# Revit family: PV_Compact_PN25_DN080_(20-100kPa)_RFA_2018
name_source: partatom
category: Pipe Accessories
revit_build: Autodesk Revit LT 2018 (Build: 20180329_1100(x64)
units: mm (PartAtom-declared; Revit-internal decimal feet)

## family parameters
Always vertical = Yes
Cut with Voids When Loaded = No
Part Type = Valve - Breaks Into
Round Connector Dimension = Use Diameter
Shared = No
Work Plane-Based = No

## types (7) — shared parameters
CAT0 = Yes
Description = Nastavitelný regulátor tlakové diference
L2D = 230 mm
L2D_Min = 30 mm  [stored 0.0984252 ft]
MC Pressure Drop Maximum Value = 0.0 Pa
MC Pressure Drop Minimum Value = 0.0 Pa
MC Use Limits From Balancing Method = No
Manufacturer = Hydronic Systems Prague s.r.o.
QmdConnectorList = 301;D;302;D
URL = www.hydronic.cz
W2D = 50 mm  [stored 0.164042 ft]
magiPartTypeId = 304
magiProductFamilyId = 7c5767a2a396495b8f1e69654734b4
zero-valued in all types: MC Throttling Maximum Value, MC Throttling Minimum Value

## per-type parameters (varying)
| type | D | DF2 | H1 | H2 | H3 | H4 | H6 | L2 | L3 | L4 | LF | LF2 | LF__ve | MC Product Code | R1 | R3 | R4 | Type Comments | magiProductId |
| PV Compact PN25 DN050 (20-100kPa) | 50 mm | 83 mm | 124 mm | 62 mm | 21 mm | 25 mm  [stored 0.082021 ft] | 82 mm | 115 mm | 193 mm | 108 mm | 18 mm | 9 mm  [stored 0.0295276 ft] | -18 mm | 53-3320 DN050 PN25; nastavitelný rozsah dp=20~100kPa; Q=3,2~13,0 m3/h;  kvs=29 | 58 mm | 43 mm | 40 mm | PŘÍRUBOVÝ; PN25; dpmax=1000kPa; -10~+120°C | c83fbc6219d94d148ccf13b963e54b |
| PV Compact PN25 DN065 (20-100kPa) | 65 mm | 93 mm | 139 mm | 69 mm | 23 mm | 28 mm  [stored 0.0918635 ft] | 105 mm | 145 mm | 244 mm | 136 mm | 23 mm | 12 mm  [stored 0.0393701 ft] | -23 mm | 53-3323 DN065 PN25; nastavitelný rozsah dp=20~100kPa; Q=4,7~18,8 m3/h;  kvs=42 | 73 mm | 48 mm  [stored 0.15748 ft] | 51 mm | PŘÍRUBOVÝ; PN25; dpmax=1000kPa; -10~+120°C | 130d70b5f9404660882d0b277b908a |
| PV Compact PN25 DN080 (20-100kPa) | 80 mm | 100 mm | 150 mm | 75 mm | 25 mm  [stored 0.082021 ft] | 30 mm  [stored 0.0984252 ft] | 141 mm | 155 mm | 260 mm | 146 mm | 25 mm  [stored 0.082021 ft] | 12 mm  [stored 0.0393701 ft] | -25 mm | 53-3326 DN080 PN25; nastavitelný rozsah dp=20~100kPa; Q=7,5~30,0 m3/h;  kvs=67 | 78 mm | 52 mm  [stored 0.170604 ft] | 54 mm | PŘÍRUBOVÝ; PN25; dpmax=1000kPa; -10~+120°C | a1826ed98cb744f2bf0249353d27a7 |
| PV Compact PN25 DN100 (20-100kPa) | 100 mm | 118 mm | 176 mm | 88 mm | 29 mm | 35 mm | 235 mm | 175 mm | 294 mm | 165 mm | 28 mm  [stored 0.0918635 ft] | 14 mm  [stored 0.0459318 ft] | -28 mm  [stored -0.0918635 ft] | 53-3329 DN100 PN25; nastavitelný rozsah dp=20~100kPa; Q=12,9~51,4 m3/h;  kvs=115 | 88 mm | 61 mm | 61 mm | PŘÍRUBOVÝ; PN25; dpmax=1000kPa; -10~+120°C | 7cf36ffc9d0642d6874cd3d421d477 |
| PV Compact PN25 DN125 (20-100kPa) | 125 mm | 135 mm | 203 mm | 101 mm | 34 mm | 41 mm | 226 mm | 200 mm | 336 mm | 188 mm | 32 mm  [stored 0.104987 ft] | 16 mm  [stored 0.0524934 ft] | -32 mm  [stored -0.104987 ft] | 53-3332 DN125 PN25; nastavitelný rozsah dp=20~100kPa; Q=19,0~76,0 m3/h;  kvs=170 | 100 mm | 70 mm  [stored 0.229659 ft] | 70 mm  [stored 0.229659 ft] | PŘÍRUBOVÝ; PN25; dpmax=1000kPa; -10~+120°C | 79fb1938054147a099bb761cc75d0a |
| PV Compact PN25 DN150 (20-100kPa) | 150 mm | 143 mm | 214 mm | 107 mm | 36 mm | 43 mm | 256 mm | 240 mm | 403 mm | 226 mm | 38 mm | 19 mm | -38 mm | 53-3335 DN150 PN25; nastavitelný rozsah dp=20~100kPa; Q=28,0~112 m3/h;  kvs=250 | 120 mm | 74 mm | 84 mm | PŘÍRUBOVÝ; PN25; dpmax=1000kPa; -10~+110°C | 9089b5560db447c5b770287446c8b2 |
| PV Compact PN25 DN200 (20-100kPa) | 200 mm | 190 mm | 285 mm | 143 mm | 48 mm  [stored 0.15748 ft] | 57 mm | 150 mm | 300 mm | 504 mm | 282 mm | 48 mm  [stored 0.15748 ft] | 24 mm  [stored 0.0787402 ft] | -48 mm  [stored -0.15748 ft] | 53-3338 DN200 PN25; nastavitelný rozsah dp=20~100kPa; Q=30,7~123 m3/h;  kvs=275 | 150 mm | 99 mm | 105 mm | PŘÍRUBOVÝ; PN25; dpmax=1000kPa; -10~+110°C | 21d4a96559b243fabb2a9fe74f4fa1 |

note: [stored X ft] marks values corroborated as IEEE doubles in the binary element streams (Revit-internal decimal feet)

## geometry (parser evidence)
native form markers: Sweep x1
no freeform markers — native parametric forms only
